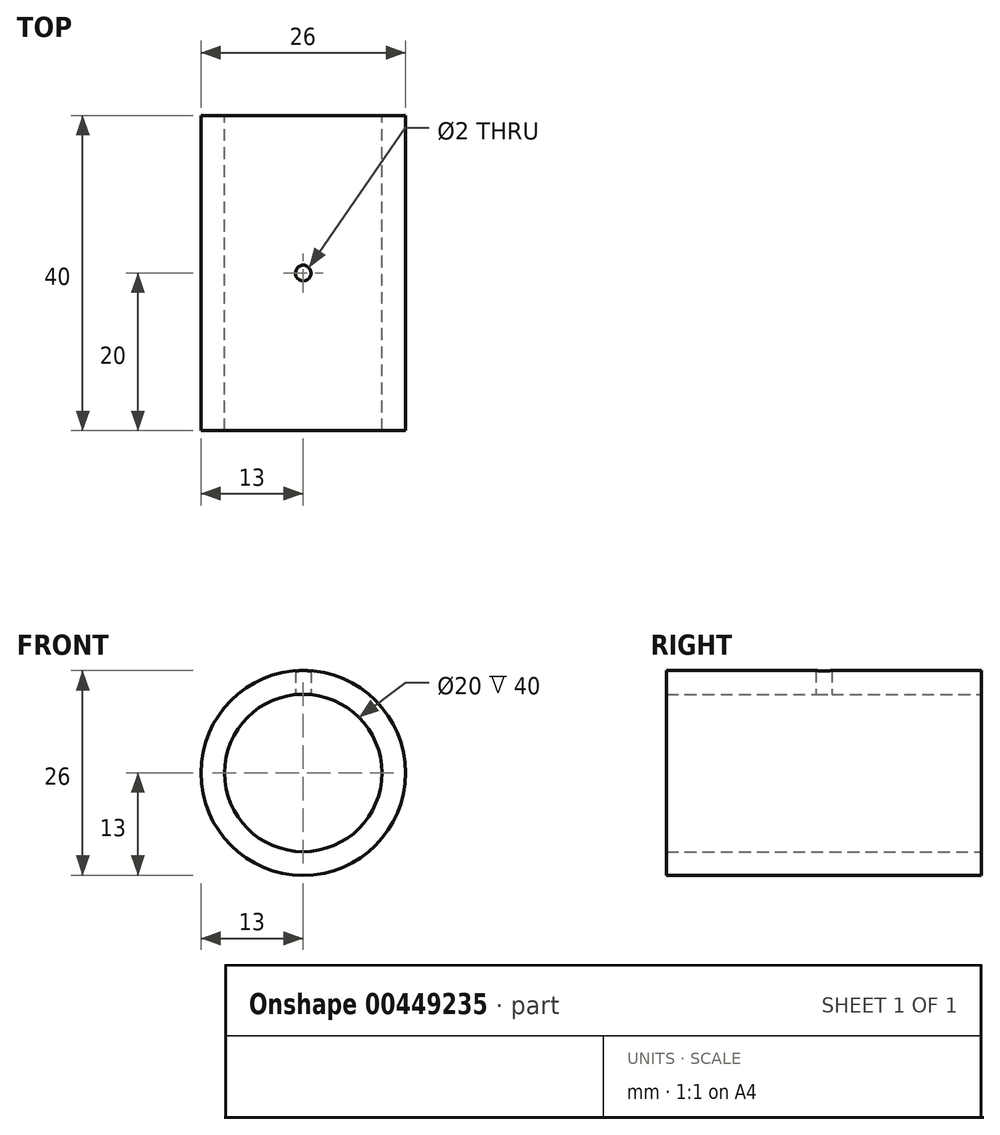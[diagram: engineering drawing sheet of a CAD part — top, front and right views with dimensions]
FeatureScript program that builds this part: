
annotation { "Feature Type Name" : "Feature", "Feature Type Description" : "" }
export const myFeature = defineFeature(function(context is Context, id is Id, definition is map)
    precondition{}
    {
        {
            var Q0;
            Q0=qCreatedBy(makeId("Front.planeOp"),FACE);
            var sketch = newSketch(context, id + "F0", { "sketchPlane" : qUnion([Q0])});
            skCircle(sketch, "E0", {"center": v(0, 0) * mm, "radius": 13 * mm});
            skCircle(sketch, "E1", {"center": v(0, 0) * mm, "radius": 10 * mm});
            skSolve(sketch);
        }
        {
            var Q0;
            Q0 = qSketchRegion(id + "F0", true);
            extrude(context, id + "F1", {"entities" : qUnion([Q0]), "depth" : 40 * mm, "symmetric" : true});
        }
        {
            var Q0;
            Q0=qCreatedBy(makeId("Top.planeOp"),FACE);
            var sketch = newSketch(context, id + "F2", { "sketchPlane" : qUnion([Q0])});
            skCircle(sketch, "E2", {"center": v(0, 0) * mm, "radius": 1 * mm});
            skSolve(sketch);
        }
        {
            var Q0;
            Q0 = qSketchRegion(id + "F2", true);
            extrude(context, id + "F3", {"entities" : qUnion([Q0]), "operationType" : NewBodyOperationType.REMOVE, "endBound" : BoundingType.THROUGH_ALL, "depth" : 25 * mm});
        }
    });
